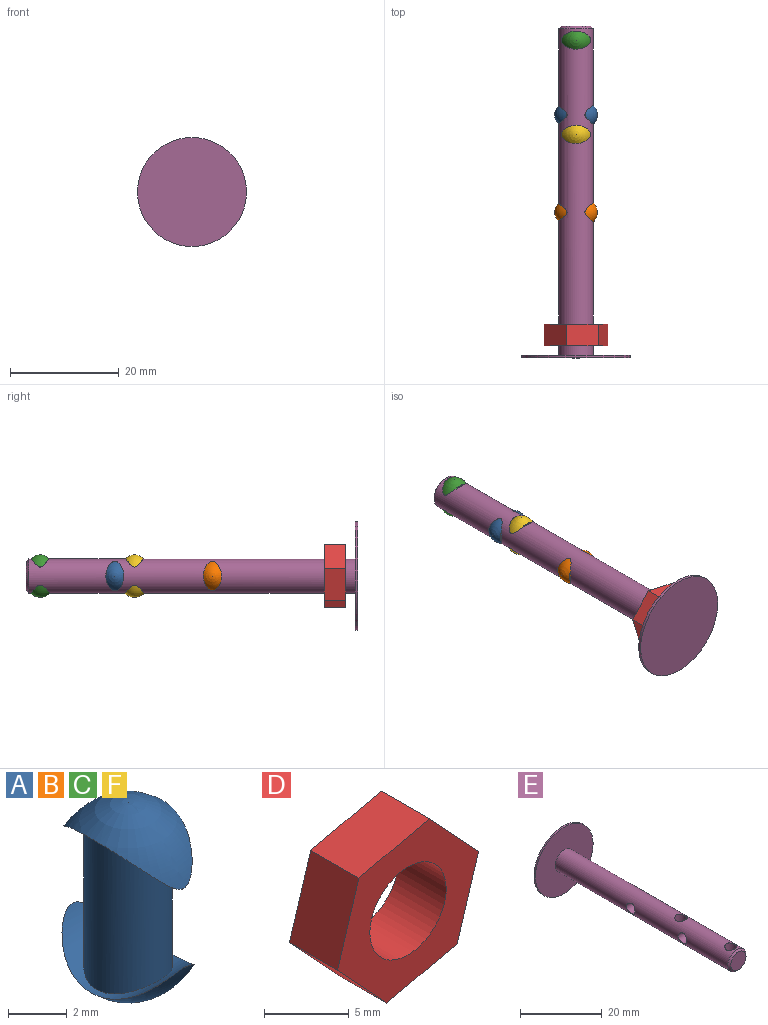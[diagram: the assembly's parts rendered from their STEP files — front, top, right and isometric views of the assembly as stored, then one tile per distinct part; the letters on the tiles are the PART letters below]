
ASSEMBLY  parts=6 mates=5
PART A: 5 faces, bbox 5.4x5.4x7.8 mm
  f0: cylinder r=3.15mm len=5.37mm, axis (-1,0,0), area 9.4mm2, adj f1,f2
  f1: revolved ~5.37x5.37mm, area 20.6mm2, adj f0
  f2: cylinder r=1.5mm len=6.3mm, axis (0,0,-1), area 59.4mm2, adj f0,f3
  f3: cylinder r=3.15mm len=5.37mm, axis (-1,0,0), area 7.9mm2, adj f2,f4
  f4: revolved ~5.37x5.37mm, area 18.5mm2, adj f3
PART B: same geometry as A
PART C: same geometry as A
PART D: 9 faces, bbox 11.7x4x11.5 mm
  f0: plane 5.87x4mm, normal (-0.22,0,0.97), area 24.1mm2, adj f1,f6,f7,f8
  f1: plane 5.76x4mm, normal (-0.96,0,0.29), area 24.1mm2, adj f0,f2,f7,f8
  f2: plane 4.41x4.1mm, normal (-0.73,0,-0.68), area 24.1mm2, adj f1,f3,f7,f8
  f3: plane 5.87x4mm, normal (0.22,0,-0.97), area 24.1mm2, adj f2,f4,f7,f8
  f4: plane 5.76x4mm, normal (0.96,0,-0.29), area 24.1mm2, adj f3,f6,f7,f8
  f5: cylinder r=3.17mm len=6.35mm, axis (0,1,0), area 79.8mm2, adj f7,f8
  f6: plane 4.41x4.1mm, normal (0.73,0,0.68), area 24.1mm2, adj f0,f4,f7,f8
  f7: plane 11.74x11.51mm, normal (0,-1,0), area 62.5mm2, adj f0,f1,f2,f3,f4,f5,f6
  f8: plane 11.74x11.51mm, normal (0,1,0), area 62.5mm2, adj f0,f1,f2,f3,f4,f5,f6
PART E: 10 faces, bbox 20x60.9x20 mm
  f0: cylinder r=3.15mm len=59.9mm, axis (0,1,0), area 1127.3mm2, adj f4,f5,f6,f7,f8,f9
  f1: plane 5.3x5.3mm, normal (0,-1,0), area 22.1mm2, adj f5
  f2: cylinder r=10mm len=20mm, axis (0,-1,0), area 31.4mm2, adj f3,f4
  f3: plane 20x20mm, normal (0,1,0), area 314.2mm2, adj f2
  f4: plane 20x20mm, normal (0,-1,0), area 283mm2, adj f0,f2
  f5: cone r=2.65mm half-angle=45deg, axis (0,1,0), area 12.9mm2, adj f0,f1
  f6: cylinder r=1.5mm len=6.3mm, axis (0,0,1), area 55.9mm2, adj f0
  f7: cylinder r=1.5mm len=6.3mm, axis (0,0,1), area 55.9mm2, adj f0
  f8: cylinder r=1.5mm len=6.3mm, axis (-1,0,0), area 55.9mm2, adj f0
  f9: cylinder r=1.5mm len=6.3mm, axis (-1,0,0), area 55.9mm2, adj f0
PART F: same geometry as A
PLACE A rot(axis=(0.58,-0.58,-0.58),120deg) t=(183.74,40.95,-174.84)mm
PLACE B rot(axis=(0.58,-0.58,-0.58),120deg) t=(183.74,23.05,-174.84)mm
PLACE C rot(axis=(0,0,-1),90deg) t=(180.59,54.65,-177.98)mm
PLACE D rot(axis=(0,0,1),180deg) t=(180.59,-1.45,-174.84)mm
PLACE E rot(axis=(0,0,1),180deg) t=(180.59,-3.15,-174.84)mm
PLACE F rot(axis=(0,0,-1),90deg) t=(180.59,37.35,-177.98)mm
MATE fastened C.f2 <-> E.f7  axis (0,0,-1) through (180.59,54.65,-174.83)mm
MATE fastened F.f2 <-> E.f6  axis (0,0,-1) through (180.59,37.35,-174.83)mm
MATE fastened B.f2 <-> E.f8  axis (1,0,0) through (180.59,23.05,-174.84)mm
MATE fastened A.f2 <-> E.f9  axis (1,0,0) through (180.59,40.95,-174.84)mm
MATE fastened D.f5 <-> E.f0  axis (0,-1,0) through (180.59,-1.45,-174.84)mm
